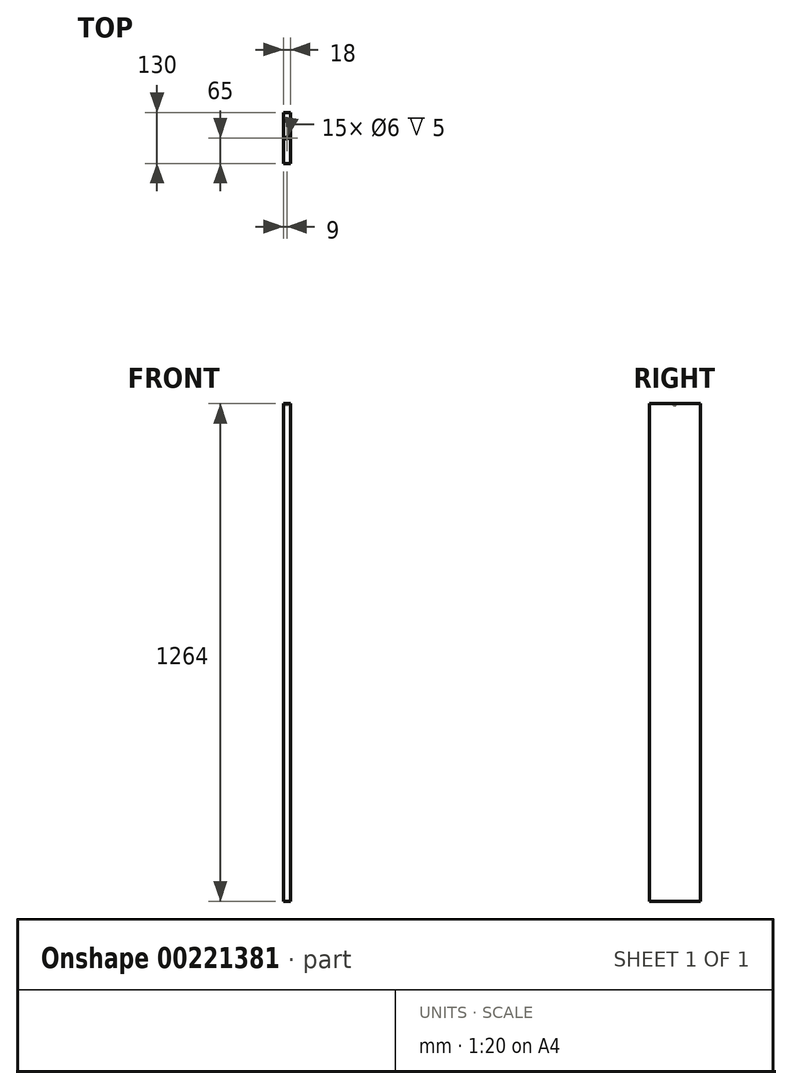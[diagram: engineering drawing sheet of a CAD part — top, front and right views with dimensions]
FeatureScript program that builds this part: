
annotation { "Feature Type Name" : "Feature", "Feature Type Description" : "" }
export const myFeature = defineFeature(function(context is Context, id is Id, definition is map)
    precondition{}
    {
        {
            var Q0;
            Q0=qCreatedBy(makeId("Right.planeOp"),FACE);
            var sketch = newSketch(context, id + "F0", { "sketchPlane" : qUnion([Q0])});
            skLineSegment(sketch, "E0.bottom", {"start": v(65, -632) * mm, "end": v(-65, -632) * mm});
            skLineSegment(sketch, "E0.top", {"start": v(65, 632) * mm, "end": v(-65, 632) * mm});
            skLineSegment(sketch, "E0.left", {"start": v(65, -632) * mm, "end": v(65, 632) * mm});
            skLineSegment(sketch, "E0.right", {"start": v(-65, -632) * mm, "end": v(-65, 632) * mm});
            skPoint(sketch, "E0.middle", {"position": v(0, 0) * mm});
            skSolve(sketch);
        }
        {
            var Q0;
            Q0 = qSketchRegion(id + "F0", true);
            extrude(context, id + "F1", {"entities" : qUnion([Q0]), "depth" : 18 * mm});
        }
        {
            var Q0;
            Q0=makeQuery(id+"F1.opExtrude","SWEPT_FACE",FACE,{"disambiguationData":[OSD([sQuery(id+"F0.wireOp",EDGE,"E0.top")])]});
            var sketch = newSketch(context, id + "F2", { "sketchPlane" : qUnion([Q0])});
            skCircle(sketch, "E1", {"center": v(9, 0) * mm, "radius": 3 * mm});
            skSolve(sketch);
        }
        {
            var Q0;
            Q0 = qSketchRegion(id + "F2", true);
            extrude(context, id + "F3", {"entities" : qUnion([Q0]), "operationType" : NewBodyOperationType.REMOVE, "oppositeDirection" : true, "depth" : 5 * mm});
        }
    });
